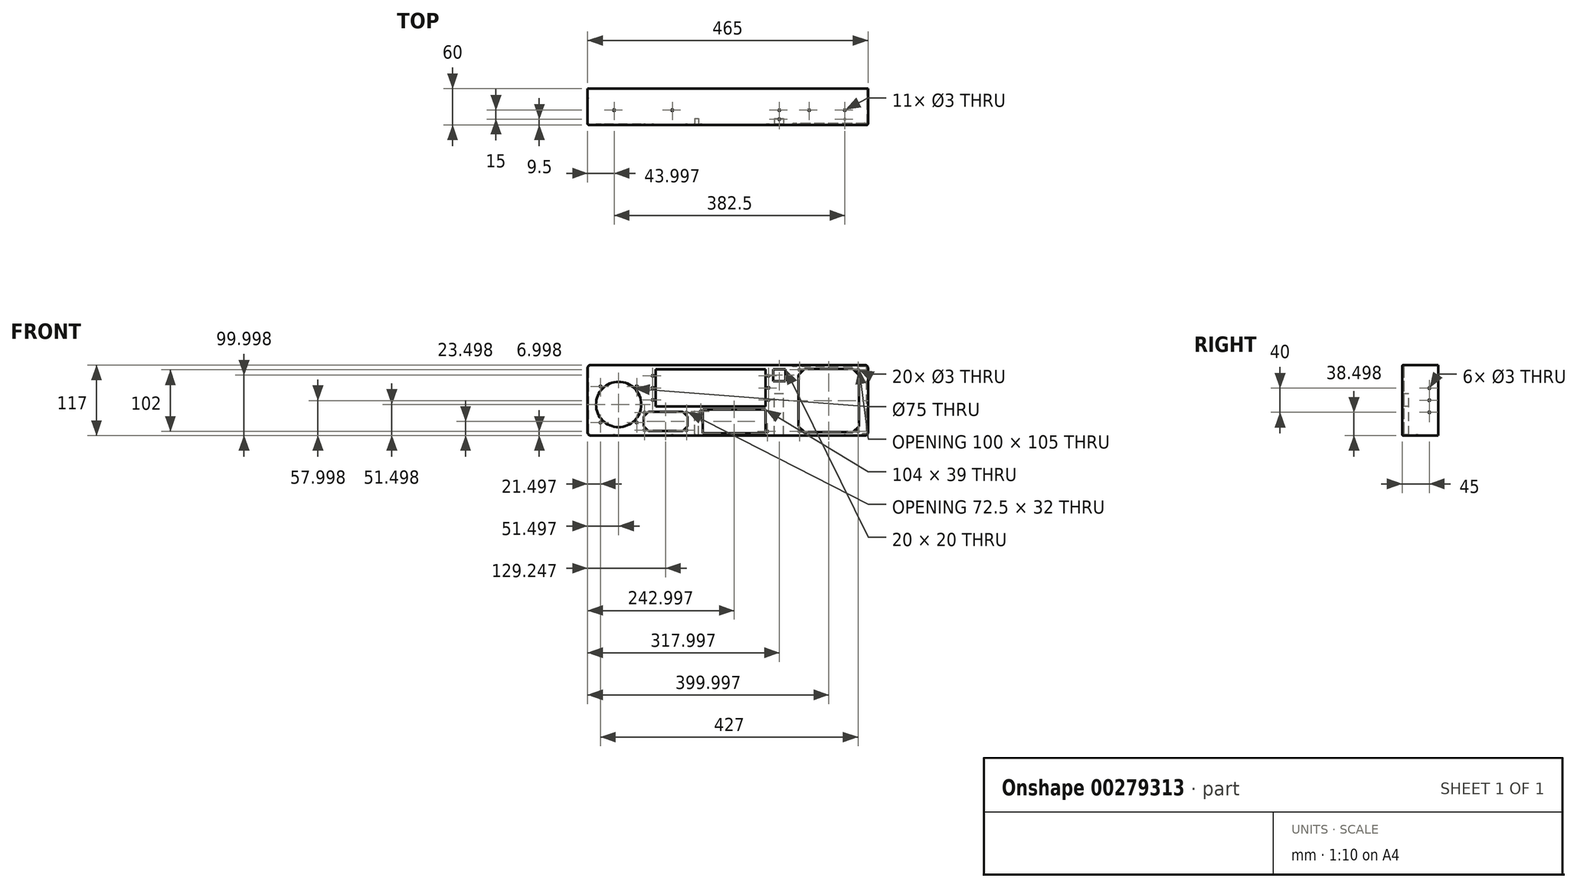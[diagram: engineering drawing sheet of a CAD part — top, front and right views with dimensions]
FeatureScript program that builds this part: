
annotation { "Feature Type Name" : "Feature", "Feature Type Description" : "" }
export const myFeature = defineFeature(function(context is Context, id is Id, definition is map)
    precondition{}
    {
        {
            var Q0;
            Q0=qCreatedBy(makeId("Front.planeOp"),FACE);
            var sketch = newSketch(context, id + "F0", { "sketchPlane" : qUnion([Q0])});
            skLineSegment(sketch, "E0.bottom", {"start": v(-245.15, 85.69) * mm, "end": v(219.85, 85.69) * mm});
            skLineSegment(sketch, "E0.top", {"start": v(-245.15, -31.31) * mm, "end": v(219.85, -31.31) * mm});
            skLineSegment(sketch, "E0.left", {"start": v(-245.15, 85.69) * mm, "end": v(-245.15, -31.31) * mm});
            skLineSegment(sketch, "E0.right", {"start": v(219.85, 85.69) * mm, "end": v(219.85, -31.31) * mm});
            skSolve(sketch);
        }
        {
            var Q0;
            Q0=qSketchRegion(id+"F0",true);
            var Q1;
            Q1=makeQuery(id+"F0.imprint","IMPRINT",FACE,{"disambiguationData":[TD([[makeQuery(id+"F0.imprint","IMPRINT",EDGE,{"derivedFrom":sQuery(id+"F0.wireOp",EDGE,"E0.bottom")}),-1.0]])]});
            extrude(context, id + "F1", {"entities" : qUnion([Q0, Q1]), "depth" : 60 * mm});
        }
        {
            var Q0;
            Q0=makeQuery(id+"F1.opExtrude","CAP_FACE",FACE,{"disambiguationData":[OSD([sQuery(id+"F0.wireOp",EDGE,"E0.bottom"),sQuery(id+"F0.wireOp",EDGE,"E0.top"),sQuery(id+"F0.wireOp",EDGE,"E0.left"),sQuery(id+"F0.wireOp",EDGE,"E0.right")])],"isStart":true});
            shell(context, id + "F2", {"entities" : qUnion([Q0]), "thickness" : 1 * mm});
        }
        {
            var Q0;
            Q0=makeQuery(id+"F1.opExtrude","CAP_FACE",FACE,{"disambiguationData":[OSD([sQuery(id+"F0.wireOp",EDGE,"E0.bottom"),sQuery(id+"F0.wireOp",EDGE,"E0.top"),sQuery(id+"F0.wireOp",EDGE,"E0.left"),sQuery(id+"F0.wireOp",EDGE,"E0.right")])],"isStart":false});
            var sketch = newSketch(context, id + "F3", { "sketchPlane" : qUnion([Q0])});
            skLineSegment(sketch, "E1.bottom", {"start": v(-132.15, 78.69) * mm, "end": v(49.85, 78.69) * mm});
            skLineSegment(sketch, "E1.top", {"start": v(-132.15, 16.69) * mm, "end": v(49.85, 16.69) * mm});
            skLineSegment(sketch, "E1.left", {"start": v(-132.15, 78.69) * mm, "end": v(-132.15, 16.69) * mm});
            skLineSegment(sketch, "E1.right", {"start": v(49.85, 78.69) * mm, "end": v(49.85, 16.69) * mm});
            skLineSegment(sketch, "E2.bottom", {"start": v(62.85, 78.69) * mm, "end": v(82.85, 78.69) * mm});
            skLineSegment(sketch, "E2.top", {"start": v(62.85, 58.69) * mm, "end": v(82.85, 58.69) * mm});
            skLineSegment(sketch, "E2.left", {"start": v(62.85, 78.69) * mm, "end": v(62.85, 58.69) * mm});
            skLineSegment(sketch, "E2.right", {"start": v(82.85, 78.69) * mm, "end": v(82.85, 58.69) * mm});
            skLineSegment(sketch, "E3.bottom", {"start": v(114.85, 79.19) * mm, "end": v(194.85, 79.19) * mm});
            skLineSegment(sketch, "E3.top", {"start": v(114.85, -25.81) * mm, "end": v(194.85, -25.81) * mm});
            skLineSegment(sketch, "E3.left", {"start": v(104.85, 69.19) * mm, "end": v(104.85, -15.81) * mm});
            skLineSegment(sketch, "E3.right", {"start": v(204.85, 69.19) * mm, "end": v(204.85, -15.81) * mm});
            skCircle(sketch, "E4", {"center": v(54.85, 67.69) * mm, "radius": 1.5 * mm});
            skCircle(sketch, "E5", {"center": v(54.85, 47.69) * mm, "radius": 1.5 * mm});
            skCircle(sketch, "E6", {"center": v(54.85, 27.69) * mm, "radius": 1.5 * mm});
            skCircle(sketch, "E7", {"center": v(106.35, 77.69) * mm, "radius": 1.5 * mm});
            skLineSegment(sketch, "E8", {"start": v(104.85, 69.19) * mm, "end": v(114.85, 79.19) * mm});
            skLineSegment(sketch, "E9.bottom", {"start": v(-144.65, 8.19) * mm, "end": v(-87.15, 8.19) * mm});
            skLineSegment(sketch, "E9.top", {"start": v(-144.65, -23.81) * mm, "end": v(-87.15, -23.81) * mm});
            skLineSegment(sketch, "E9.left", {"start": v(-152.15, 0.69) * mm, "end": v(-152.15, -16.31) * mm});
            skLineSegment(sketch, "E9.right", {"start": v(-79.65, 0.69) * mm, "end": v(-79.65, -16.31) * mm});
            skLineSegment(sketch, "E10", {"start": v(104.85, -15.81) * mm, "end": v(114.85, -25.81) * mm});
            skLineSegment(sketch, "E11", {"start": v(194.85, -25.81) * mm, "end": v(204.85, -15.81) * mm});
            skLineSegment(sketch, "E12", {"start": v(194.85, 79.19) * mm, "end": v(204.85, 69.19) * mm});
            skCircle(sketch, "E13", {"center": v(-193.65, 20.19) * mm, "radius": 37.5 * mm});
            skLineSegment(sketch, "E14", {"start": v(-152.15, 0.69) * mm, "end": v(-144.65, 8.19) * mm});
            skLineSegment(sketch, "E15", {"start": v(-87.15, 8.19) * mm, "end": v(-79.65, 0.69) * mm});
            skLineSegment(sketch, "E16", {"start": v(-79.65, -16.31) * mm, "end": v(-87.15, -23.81) * mm});
            skLineSegment(sketch, "E17", {"start": v(-152.15, -16.31) * mm, "end": v(-144.65, -23.81) * mm});
            skCircle(sketch, "E18", {"center": v(-137.15, 67.69) * mm, "radius": 1.5 * mm});
            skCircle(sketch, "E19", {"center": v(-137.15, 47.69) * mm, "radius": 1.5 * mm});
            skCircle(sketch, "E20", {"center": v(-137.15, 27.69) * mm, "radius": 1.5 * mm});
            skCircle(sketch, "E21", {"center": v(-223.65, 50.19) * mm, "radius": 1.5 * mm});
            skCircle(sketch, "E22", {"center": v(-223.65, -9.81) * mm, "radius": 1.5 * mm});
            skCircle(sketch, "E23", {"center": v(-163.65, -9.81) * mm, "radius": 1.5 * mm});
            skCircle(sketch, "E24", {"center": v(-163.65, 50.19) * mm, "radius": 1.5 * mm});
            skCircle(sketch, "E25", {"center": v(-57.15, 8.69) * mm, "radius": 1.5 * mm});
            skCircle(sketch, "E26", {"center": v(52.85, -24.31) * mm, "radius": 1.5 * mm});
            skLineSegment(sketch, "E27.bottom", {"start": v(-54.15, 11.69) * mm, "end": v(49.85, 11.69) * mm});
            skLineSegment(sketch, "E27.top", {"start": v(-54.15, -27.31) * mm, "end": v(49.85, -27.31) * mm});
            skLineSegment(sketch, "E27.left", {"start": v(-54.15, 11.69) * mm, "end": v(-54.15, -27.31) * mm});
            skLineSegment(sketch, "E27.right", {"start": v(49.85, 11.69) * mm, "end": v(49.85, -27.31) * mm});
            skLineSegment(sketch, "E28.bottom", {"start": v(-163.65, -9.81) * mm, "end": v(-223.65, -9.81) * mm, "construction": true});
            skLineSegment(sketch, "E28.top", {"start": v(-163.65, 50.19) * mm, "end": v(-223.65, 50.19) * mm, "construction": true});
            skLineSegment(sketch, "E28.left", {"start": v(-163.65, -9.81) * mm, "end": v(-163.65, 50.19) * mm, "construction": true});
            skLineSegment(sketch, "E28.right", {"start": v(-223.65, -9.81) * mm, "end": v(-223.65, 50.19) * mm, "construction": true});
            skCircle(sketch, "E29", {"center": v(-150.65, 6.69) * mm, "radius": 1.5 * mm});
            skCircle(sketch, "E30", {"center": v(-81.15, 6.69) * mm, "radius": 1.5 * mm});
            skCircle(sketch, "E31", {"center": v(-150.65, -22.31) * mm, "radius": 1.5 * mm});
            skCircle(sketch, "E32", {"center": v(-81.15, -22.31) * mm, "radius": 1.5 * mm});
            skCircle(sketch, "E33", {"center": v(203.35, 77.69) * mm, "radius": 1.5 * mm});
            skCircle(sketch, "E34", {"center": v(106.35, -24.31) * mm, "radius": 1.5 * mm});
            skCircle(sketch, "E35", {"center": v(203.35, -24.31) * mm, "radius": 1.5 * mm});
            skSolve(sketch);
        }
        {
            var Q0;
            Q0=qSketchRegion(id+"F3",true);
            extrude(context, id + "F4", {"entities" : qUnion([Q0]), "operationType" : NewBodyOperationType.REMOVE, "oppositeDirection" : true, "depth" : 25 * mm});
        }
        {
            var Q0;
            Q0=makeQuery(id+"F1.opExtrude","SWEPT_FACE",FACE,{"disambiguationData":[OSD([sQuery(id+"F0.wireOp",EDGE,"E0.left")])]});
            var sketch = newSketch(context, id + "F5", { "sketchPlane" : qUnion([Q0])});
            skCircle(sketch, "E36", {"center": v(15, 47.19) * mm, "radius": 1.5 * mm});
            skCircle(sketch, "E37", {"center": v(15, 7.19) * mm, "radius": 1.5 * mm});
            skLineSegment(sketch, "E38", {"start": v(-16.01, 27.19) * mm, "end": v(37.35, 27.19) * mm, "construction": true});
            skPoint(sketch, "E39.middle.positionSnap0", {"position": v(0, 27.19) * mm});
            skPoint(sketch, "E39.centerSnap0", {"position": v(0, 27.19) * mm});
            skCircle(sketch, "E40", {"center": v(15, 27.19) * mm, "radius": 1.5 * mm});
            skSolve(sketch);
        }
        {
            var Q0;
            Q0=qSketchRegion(id+"F5",true);
            extrude(context, id + "F6", {"entities" : qUnion([Q0]), "operationType" : NewBodyOperationType.REMOVE, "oppositeDirection" : true, "depth" : 500 * mm});
        }
        {
            var Q0;
            Q0=makeQuery(id+"F1.opExtrude","SWEPT_FACE",FACE,{"disambiguationData":[OSD([sQuery(id+"F0.wireOp",EDGE,"E0.bottom")])]});
            var sketch = newSketch(context, id + "F7", { "sketchPlane" : qUnion([Q0])});
            skCircle(sketch, "E41", {"center": v(-201.15, -35.5) * mm, "radius": 1.5 * mm});
            skCircle(sketch, "E42", {"center": v(-104.65, -35.5) * mm, "radius": 1.5 * mm});
            skCircle(sketch, "E43", {"center": v(122.35, -35.5) * mm, "radius": 1.5 * mm});
            skCircle(sketch, "E44", {"center": v(181.35, -35.5) * mm, "radius": 1.5 * mm});
            skCircle(sketch, "E45", {"center": v(72.85, -35.5) * mm, "radius": 1.5 * mm});
            skCircle(sketch, "E46", {"center": v(72.85, -50.5) * mm, "radius": 1.5 * mm});
            skCircle(sketch, "E47", {"center": v(181.35, -50.5) * mm, "radius": 1.5 * mm, "construction": true});
            skSolve(sketch);
        }
        {
            var Q0;
            Q0=makeQuery(id+"F7.imprint","IMPRINT",FACE,{"disambiguationData":[TD([[makeQuery(id+"F7.imprint","IMPRINT",EDGE,{"derivedFrom":sQuery(id+"F7.wireOp",EDGE,"E41")}),1.0]])]});
            var Q1;
            Q1=makeQuery(id+"F7.imprint","IMPRINT",FACE,{"disambiguationData":[TD([[makeQuery(id+"F7.imprint","IMPRINT",EDGE,{"derivedFrom":sQuery(id+"F7.wireOp",EDGE,"E42")}),1.0]])]});
            var Q2;
            Q2=makeQuery(id+"F7.imprint","IMPRINT",FACE,{"disambiguationData":[TD([[makeQuery(id+"F7.imprint","IMPRINT",EDGE,{"derivedFrom":sQuery(id+"F7.wireOp",EDGE,"E43")}),1.0]])]});
            var Q3;
            Q3=makeQuery(id+"F7.imprint","IMPRINT",FACE,{"disambiguationData":[TD([[makeQuery(id+"F7.imprint","IMPRINT",EDGE,{"derivedFrom":sQuery(id+"F7.wireOp",EDGE,"E44")}),1.0]])]});
            var Q4;
            Q4=makeQuery(id+"F7.imprint","IMPRINT",FACE,{"disambiguationData":[TD([[makeQuery(id+"F7.imprint","IMPRINT",EDGE,{"derivedFrom":sQuery(id+"F7.wireOp",EDGE,"E47")}),1.0]])]});
            extrude(context, id + "F8", {"entities" : qUnion([Q0, Q1, Q2, Q3, Q4]), "operationType" : NewBodyOperationType.REMOVE, "endBound" : BoundingType.THROUGH_ALL, "oppositeDirection" : true, "depth" : 117 * mm});
        }
        {
            var Q0;
            Q0=makeQuery(id+"F7.imprint","IMPRINT",FACE,{"disambiguationData":[TD([[makeQuery(id+"F7.imprint","IMPRINT",EDGE,{"derivedFrom":sQuery(id+"F7.wireOp",EDGE,"E45")}),1.0]])]});
            var Q1;
            Q1=makeQuery(id+"F7.imprint","IMPRINT",FACE,{"disambiguationData":[TD([[makeQuery(id+"F7.imprint","IMPRINT",EDGE,{"derivedFrom":sQuery(id+"F7.wireOp",EDGE,"E46")}),1.0]])]});
            extrude(context, id + "F9", {"entities" : qUnion([Q0, Q1]), "operationType" : NewBodyOperationType.REMOVE, "oppositeDirection" : true, "depth" : 2 * mm});
        }
        {
            var Q0;
            Q0=makeQuery(id+"F1.opExtrude","SWEPT_FACE",FACE,{"disambiguationData":[OSD([sQuery(id+"F0.wireOp",EDGE,"E0.top")])]});
            var sketch = newSketch(context, id + "F10", { "sketchPlane" : qUnion([Q0])});
            skCircle(sketch, "E48", {"center": v(181.35, 50.5) * mm, "radius": 1.5 * mm});
            skCircle(sketch, "E49.0", {"center": v(181.35, 35.5) * mm, "radius": 1.5 * mm, "construction": true});
            skSolve(sketch);
        }
        {
            var Q0;
            Q0 = qSketchRegion(id + "F10", true);
            extrude(context, id + "F11", {"entities" : qUnion([Q0]), "operationType" : NewBodyOperationType.REMOVE, "oppositeDirection" : true, "depth" : 2 * mm});
        }
        {
            var Q0;
            Q0=makeQuery(id+"F2.opShell","OFFSET_FACE",FACE,{"disambiguationData":[OSD([sQuery(id+"F0.wireOp",EDGE,"E0.bottom"),sQuery(id+"F0.wireOp",EDGE,"E0.top"),sQuery(id+"F0.wireOp",EDGE,"E0.left"),sQuery(id+"F0.wireOp",EDGE,"E0.right")])]});
            var sketch = newSketch(context, id + "F12", { "sketchPlane" : qUnion([Q0])});
            skLineSegment(sketch, "E50.bottom", {"start": v(-79.86, -30.31) * mm, "end": v(-64.86, -30.31) * mm});
            skLineSegment(sketch, "E50.top", {"start": v(-79.86, 38.12) * mm, "end": v(-64.86, 38.12) * mm});
            skLineSegment(sketch, "E50.left", {"start": v(-79.86, -30.31) * mm, "end": v(-79.86, 38.12) * mm});
            skLineSegment(sketch, "E50.right", {"start": v(-64.86, -30.31) * mm, "end": v(-64.86, 38.12) * mm});
            skLineSegment(sketch, "E51.bottom", {"start": v(61.44, -30.31) * mm, "end": v(67.44, -30.31) * mm});
            skLineSegment(sketch, "E51.top", {"start": v(61.44, 16.69) * mm, "end": v(67.44, 16.69) * mm});
            skLineSegment(sketch, "E51.left", {"start": v(61.44, -30.31) * mm, "end": v(61.44, 16.69) * mm});
            skLineSegment(sketch, "E51.right", {"start": v(67.44, -30.31) * mm, "end": v(67.44, 16.69) * mm});
            skLineSegment(sketch, "E52.bottom", {"start": v(-64.86, 16.19) * mm, "end": v(61.44, 16.19) * mm});
            skLineSegment(sketch, "E52.top", {"start": v(-64.86, 12.19) * mm, "end": v(61.44, 12.19) * mm});
            skLineSegment(sketch, "E52.left", {"start": v(-64.86, 16.19) * mm, "end": v(-64.86, 12.19) * mm});
            skLineSegment(sketch, "E52.right", {"start": v(61.44, 16.19) * mm, "end": v(61.44, 12.19) * mm});
            skLineSegment(sketch, "E53.bottom", {"start": v(-55.88, 84.69) * mm, "end": v(244.15, 84.69) * mm});
            skLineSegment(sketch, "E53.top", {"start": v(-55.88, 81.41) * mm, "end": v(244.15, 81.41) * mm});
            skLineSegment(sketch, "E53.left", {"start": v(-55.88, 84.69) * mm, "end": v(-55.88, 81.41) * mm});
            skLineSegment(sketch, "E53.right", {"start": v(244.15, 84.69) * mm, "end": v(244.15, 81.41) * mm});
            skLineSegment(sketch, "E54.bottom", {"start": v(244.15, 81.41) * mm, "end": v(239.22, 81.41) * mm});
            skLineSegment(sketch, "E54.top", {"start": v(244.15, -30.31) * mm, "end": v(239.22, -30.31) * mm});
            skLineSegment(sketch, "E54.left", {"start": v(244.15, 81.41) * mm, "end": v(244.15, -30.31) * mm});
            skLineSegment(sketch, "E54.right", {"start": v(239.22, 81.41) * mm, "end": v(239.22, -30.31) * mm});
            skLineSegment(sketch, "E55.bottom", {"start": v(-218.85, 84.69) * mm, "end": v(-216.85, 84.69) * mm});
            skLineSegment(sketch, "E55.top", {"start": v(-218.85, -30.31) * mm, "end": v(-216.85, -30.31) * mm});
            skLineSegment(sketch, "E55.left", {"start": v(-218.85, 84.69) * mm, "end": v(-218.85, -30.31) * mm});
            skLineSegment(sketch, "E55.right", {"start": v(-216.85, 84.69) * mm, "end": v(-216.85, -30.31) * mm});
            skLineSegment(sketch, "E56.bottom", {"start": v(-216.85, -30.31) * mm, "end": v(-210.85, -30.31) * mm});
            skLineSegment(sketch, "E56.top", {"start": v(-216.85, -28.31) * mm, "end": v(-210.85, -28.31) * mm});
            skLineSegment(sketch, "E56.left", {"start": v(-216.85, -30.31) * mm, "end": v(-216.85, -28.31) * mm});
            skLineSegment(sketch, "E56.right", {"start": v(-210.85, -30.31) * mm, "end": v(-210.85, -28.31) * mm});
            skLineSegment(sketch, "E57.bottom", {"start": v(-216.85, 84.69) * mm, "end": v(-94.85, 84.69) * mm});
            skLineSegment(sketch, "E57.top", {"start": v(-216.85, 82.69) * mm, "end": v(-94.85, 82.69) * mm});
            skLineSegment(sketch, "E57.left", {"start": v(-216.85, 84.69) * mm, "end": v(-216.85, 82.69) * mm});
            skLineSegment(sketch, "E57.right", {"start": v(-94.85, 84.69) * mm, "end": v(-94.85, 82.69) * mm});
            skLineSegment(sketch, "E58.bottom", {"start": v(-94.85, 82.69) * mm, "end": v(-96.85, 82.69) * mm});
            skLineSegment(sketch, "E58.top", {"start": v(-94.85, -30.31) * mm, "end": v(-96.85, -30.31) * mm});
            skLineSegment(sketch, "E58.left", {"start": v(-94.85, 82.69) * mm, "end": v(-94.85, -30.31) * mm});
            skLineSegment(sketch, "E58.right", {"start": v(-96.85, 82.69) * mm, "end": v(-96.85, -30.31) * mm});
            skSolve(sketch);
        }
        {
            var Q0;
            {var subQ1=sQuery(id+"F12.wireOp",EDGE,"E50.bottom");Q0=makeQuery(id+"F12.imprint","IMPRINT",FACE,{"disambiguationData":[TD([[makeQuery(id+"F12.imprint","IMPRINT",EDGE,{"derivedFrom":subQ1}),-1.0]])]});}
            var Q1;
            {var subQ4=sQuery(id+"F12.wireOp",EDGE,"E51.bottom");Q1=makeQuery(id+"F12.imprint","IMPRINT",FACE,{"disambiguationData":[TD([[makeQuery(id+"F12.imprint","IMPRINT",EDGE,{"derivedFrom":subQ4}),-1.0]])]});}
            extrude(context, id + "F13", {"entities" : qUnion([Q0, Q1]), "operationType" : NewBodyOperationType.ADD, "depth" : 10 * mm});
        }
        {
            var Q0;
            Q0=makeQuery(id+"F12.imprint","IMPRINT",FACE,{"disambiguationData":[TD([[makeQuery(id+"F12.imprint","IMPRINT",EDGE,{"derivedFrom":sQuery(id+"F12.wireOp",EDGE,"E55.bottom")}),1.0]])]});
            var Q1;
            Q1=makeQuery(id+"F12.imprint","IMPRINT",FACE,{"disambiguationData":[TD([[makeQuery(id+"F12.imprint","IMPRINT",EDGE,{"derivedFrom":sQuery(id+"F12.wireOp",EDGE,"E56.bottom")}),-1.0]])]});
            var Q2;
            Q2=makeQuery(id+"F12.imprint","IMPRINT",FACE,{"disambiguationData":[TD([[makeQuery(id+"F12.imprint","IMPRINT",EDGE,{"derivedFrom":sQuery(id+"F12.wireOp",EDGE,"E57.bottom")}),1.0]])]});
            extrude(context, id + "F14", {"entities" : qUnion([Q0, Q1, Q2]), "operationType" : NewBodyOperationType.ADD, "depth" : 1.5 * mm});
        }
        {
            var Q0;
            Q0=makeQuery(id+"F1.opExtrude","SWEPT_EDGE",EDGE,{"disambiguationData":[OSD([sQuery(id+"F0.wireOp",EDGE,"E0.bottom"),sQuery(id+"F0.wireOp",EDGE,"E0.left")])]});
            var Q1;
            Q1=makeQuery(id+"F1.opExtrude","SWEPT_EDGE",EDGE,{"disambiguationData":[OSD([sQuery(id+"F0.wireOp",EDGE,"E0.bottom"),sQuery(id+"F0.wireOp",EDGE,"E0.right")])]});
            var Q2;
            Q2=makeQuery(id+"F1.opExtrude","SWEPT_EDGE",EDGE,{"disambiguationData":[OSD([sQuery(id+"F0.wireOp",EDGE,"E0.top"),sQuery(id+"F0.wireOp",EDGE,"E0.right")])]});
            var Q3;
            Q3=makeQuery(id+"F1.opExtrude","SWEPT_EDGE",EDGE,{"disambiguationData":[OSD([sQuery(id+"F0.wireOp",EDGE,"E0.top"),sQuery(id+"F0.wireOp",EDGE,"E0.left")])]});
            var Q4;
            Q4=makeQuery(id+"F2.opShell","OFFSET_EDGE",EDGE,{"disambiguationData":[OSD([sQuery(id+"F0.wireOp",EDGE,"E0.bottom"),sQuery(id+"F0.wireOp",EDGE,"E0.left")])]});
            var Q5;
            Q5=makeQuery(id+"F2.opShell","OFFSET_EDGE",EDGE,{"disambiguationData":[OSD([sQuery(id+"F0.wireOp",EDGE,"E0.top"),sQuery(id+"F0.wireOp",EDGE,"E0.left")])]});
            var Q6;
            Q6=makeQuery(id+"F2.opShell","OFFSET_EDGE",EDGE,{"disambiguationData":[OSD([sQuery(id+"F0.wireOp",EDGE,"E0.top"),sQuery(id+"F0.wireOp",EDGE,"E0.right")])]});
            var Q7;
            Q7=makeQuery(id+"F2.opShell","OFFSET_EDGE",EDGE,{"disambiguationData":[OSD([sQuery(id+"F0.wireOp",EDGE,"E0.bottom"),sQuery(id+"F0.wireOp",EDGE,"E0.right")])]});
            fillet(context, id + "F15", {"entities" : qUnion([Q0, Q1, Q2, Q3, Q4, Q5, Q6, Q7]), "radius" : 5 * mm, "tangentPropagation" : true, "allowEdgeOverflow" : false});
        }
        {
            var Q0;
            {var subQ0=sQuery(id+"F0.wireOp",EDGE,"E0.right");var subQ1=sQuery(id+"F0.wireOp",EDGE,"E0.bottom");Q0=makeQuery(id+"F15.opFillet","BLEND_EDGE",EDGE,{"blendedFrom":[makeQuery(id+"F1.opExtrude","SWEPT_EDGE",EDGE,{"disambiguationData":[OSD([subQ1,subQ0])]}),makeQuery(id+"F1.opExtrude","CAP_FACE",FACE,{"disambiguationData":[OSD([subQ1,sQuery(id+"F0.wireOp",EDGE,"E0.top"),sQuery(id+"F0.wireOp",EDGE,"E0.left"),subQ0])],"isStart":false})],"blendedInto":[makeQuery(id+"F1.opExtrude","CAP_FACE",FACE,{"disambiguationData":[OSD([subQ1,sQuery(id+"F0.wireOp",EDGE,"E0.top"),sQuery(id+"F0.wireOp",EDGE,"E0.left"),subQ0])],"isStart":false})]});}
            var Q1;
            {var subQ0=sQuery(id+"F0.wireOp",EDGE,"E0.bottom");Q1=makeQuery(id+"F2.opShell","OFFSET_EDGE",EDGE,{"disambiguationData":[OSD([subQ0]),TDD([makeQuery(id+"F1.opExtrude","CAP_EDGE",EDGE,{"disambiguationData":[OSD([subQ0])],"isStart":false})])]});}
            fillet(context, id + "F16", {"entities" : qUnion([Q0, Q1]), "radius" : 2 * mm, "tangentPropagation" : true, "allowEdgeOverflow" : false});
        }
    });
